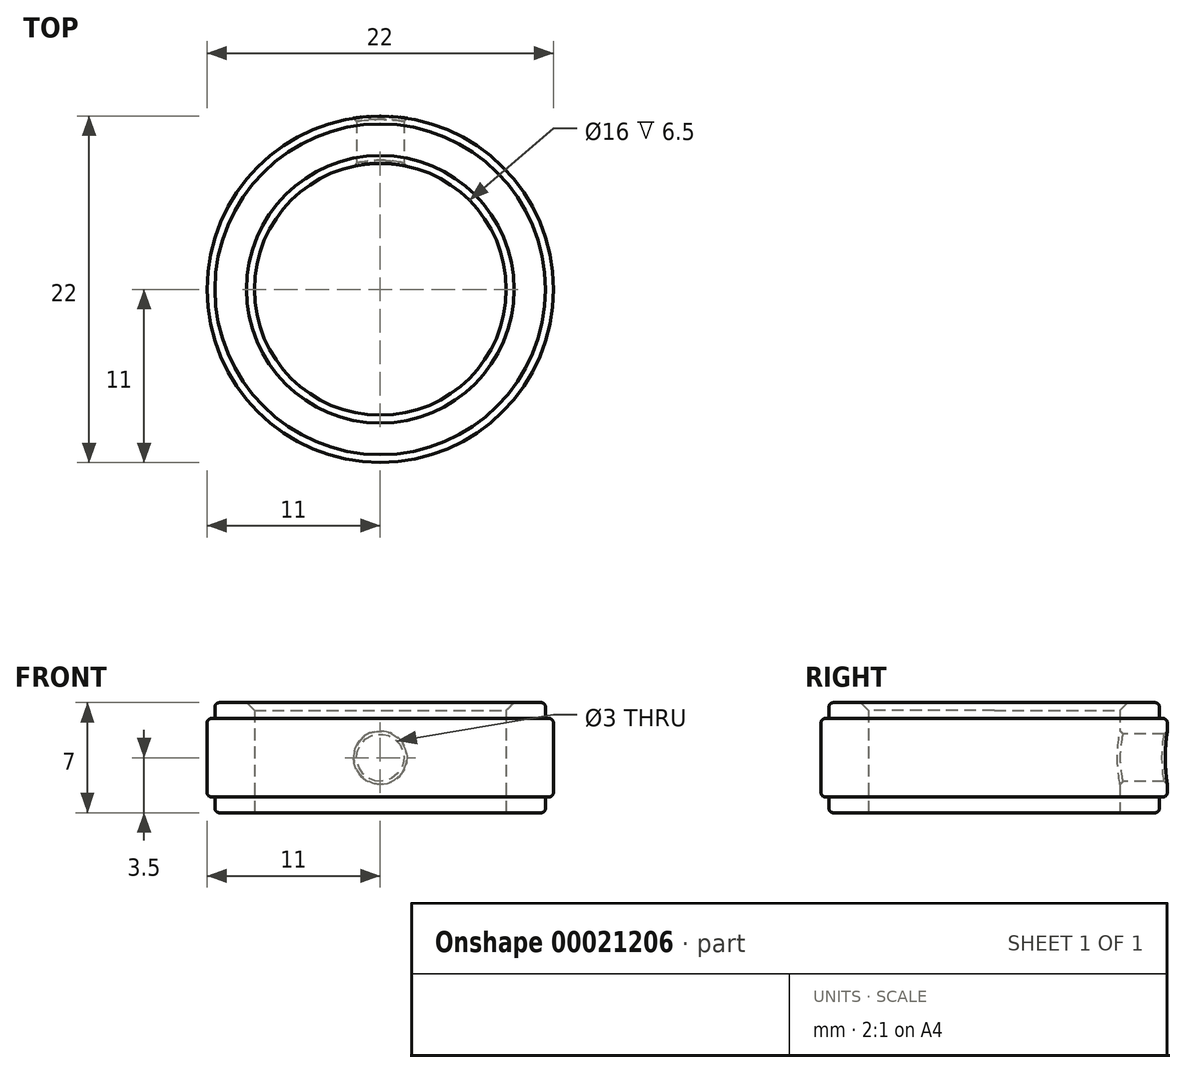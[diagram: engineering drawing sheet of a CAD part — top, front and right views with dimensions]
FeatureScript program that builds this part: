
annotation { "Feature Type Name" : "Feature", "Feature Type Description" : "" }
export const myFeature = defineFeature(function(context is Context, id is Id, definition is map)
    precondition{}
    {
        {
            var Q0;
            Q0=qCreatedBy(makeId("Top.planeOp"),FACE);
            var sketch = newSketch(context, id + "F0", { "sketchPlane" : qUnion([Q0])});
            skCircle(sketch, "E0", {"center": v(0, 0) * mm, "radius": 11 * mm});
            skSolve(sketch);
        }
        {
            var Q0;
            Q0=qSketchRegion(id+"F0",true);
            extrude(context, id + "F1", {"entities" : qUnion([Q0]), "endBound" : BoundingType.SYMMETRIC, "depth" : 5 * mm});
        }
        {
            var Q0;
            Q0=makeQuery(id+"F1.opExtrude","CAP_FACE",FACE,{"disambiguationData":[OSD([sQuery(id+"F0.wireOp",EDGE,"E0")])],"isStart":false});
            var sketch = newSketch(context, id + "F2", { "sketchPlane" : qUnion([Q0])});
            skCircle(sketch, "E1", {"center": v(0, 0) * mm, "radius": 10.5 * mm});
            skSolve(sketch);
        }
        {
            var Q0;
            Q0=qSketchRegion(id+"F2",true);
            extrude(context, id + "F3", {"entities" : qUnion([Q0]), "operationType" : NewBodyOperationType.ADD, "depth" : 1 * mm});
        }
        {
            var Q0;
            Q0=makeQuery(id+"F1.opExtrude","CAP_FACE",FACE,{"disambiguationData":[OSD([sQuery(id+"F0.wireOp",EDGE,"E0")])],"isStart":true});
            var sketch = newSketch(context, id + "F4", { "sketchPlane" : qUnion([Q0])});
            skCircle(sketch, "E2", {"center": v(0, 0) * mm, "radius": 10.5 * mm});
            skSolve(sketch);
        }
        {
            var Q0;
            Q0=qSketchRegion(id+"F4",true);
            extrude(context, id + "F5", {"entities" : qUnion([Q0]), "operationType" : NewBodyOperationType.ADD, "depth" : 1 * mm});
        }
        {
            var Q0;
            Q0=makeQuery(id+"F5.opExtrude","CAP_FACE",FACE,{"disambiguationData":[OSD([sQuery(id+"F4.wireOp",EDGE,"E2")])],"isStart":false});
            var sketch = newSketch(context, id + "F6", { "sketchPlane" : qUnion([Q0])});
            skCircle(sketch, "E3", {"center": v(0, 0) * mm, "radius": 8 * mm});
            skSolve(sketch);
        }
        {
            var Q0;
            Q0=qSketchRegion(id+"F6",true);
            extrude(context, id + "F7", {"entities" : qUnion([Q0]), "operationType" : NewBodyOperationType.REMOVE, "endBound" : BoundingType.THROUGH_ALL, "oppositeDirection" : true, "depth" : 25 * mm});
        }
        {
            var Q0;
            Q0=makeQuery(id+"F3.opExtrude","CAP_EDGE",EDGE,{"disambiguationData":[OSD([sQuery(id+"F2.wireOp",EDGE,"E1")])],"isStart":false});
            var Q1;
            Q1=makeQuery(id+"F1.opExtrude","CAP_EDGE",EDGE,{"disambiguationData":[OSD([sQuery(id+"F0.wireOp",EDGE,"E0")])],"isStart":false});
            var Q2;
            Q2=makeQuery(id+"F1.opExtrude","CAP_EDGE",EDGE,{"disambiguationData":[OSD([sQuery(id+"F0.wireOp",EDGE,"E0")])],"isStart":true});
            var Q3;
            Q3=makeQuery(id+"F5.opExtrude","CAP_EDGE",EDGE,{"disambiguationData":[OSD([sQuery(id+"F4.wireOp",EDGE,"E2")])],"isStart":false});
            fillet(context, id + "F8", {"entities" : qUnion([Q0, Q1, Q2, Q3]), "radius" : 0.3 * mm, "tangentPropagation" : true, "allowEdgeOverflow" : false});
        }
        {
            var Q0;
            Q0=makeQuery(id+"F7.boolean.opBoolean","INTERSECT",EDGE,{"derivedFrom":[makeQuery(id+"F3.opExtrude","CAP_FACE",FACE,{"disambiguationData":[OSD([sQuery(id+"F2.wireOp",EDGE,"E1")])],"isStart":false}),makeQuery(id+"F7.opExtrude","SWEPT_FACE",FACE,{"disambiguationData":[OSD([sQuery(id+"F6.wireOp",EDGE,"E3")])]})]});
            var Q1;
            Q1=makeQuery(id+"F7.boolean.opBoolean","COPY",EDGE,{"derivedFrom":makeQuery(id+"F7.opExtrude","CAP_EDGE",EDGE,{"disambiguationData":[OSD([sQuery(id+"F6.wireOp",EDGE,"E3")])],"isStart":true})});
            chamfer(context, id + "F9", {"entities" : qUnion([Q0, Q1]), "width" : 0.5 * mm, "tangentPropagation" : true});
        }
        {
            var Q0;
            Q0=qCreatedBy(makeId("Front.planeOp"),FACE);
            var sketch = newSketch(context, id + "F10", { "sketchPlane" : qUnion([Q0])});
            skCircle(sketch, "E4", {"center": v(0, 0) * mm, "radius": 1.5 * mm});
            skSolve(sketch);
        }
        {
            var Q0;
            Q0=qSketchRegion(id+"F10",true);
            extrude(context, id + "F11", {"entities" : qUnion([Q0]), "operationType" : NewBodyOperationType.REMOVE, "endBound" : BoundingType.THROUGH_ALL, "oppositeDirection" : true, "depth" : 25 * mm});
        }
        {
            var Q0;
            Q0=makeQuery(id+"F11.boolean.opBoolean","INTERSECT",EDGE,{"derivedFrom":[makeQuery(id+"F1.opExtrude","SWEPT_FACE",FACE,{"disambiguationData":[OSD([sQuery(id+"F0.wireOp",EDGE,"E0")])]}),makeQuery(id+"F11.opExtrude","SWEPT_FACE",FACE,{"disambiguationData":[OSD([sQuery(id+"F10.wireOp",EDGE,"E4")])]})]});
            var Q1;
            Q1=makeQuery(id+"F11.boolean.opBoolean","INTERSECT",EDGE,{"derivedFrom":[makeQuery(id+"F7.boolean.opBoolean","COPY",FACE,{"derivedFrom":makeQuery(id+"F7.opExtrude","SWEPT_FACE",FACE,{"disambiguationData":[OSD([sQuery(id+"F6.wireOp",EDGE,"E3")])]})}),makeQuery(id+"F11.opExtrude","SWEPT_FACE",FACE,{"disambiguationData":[OSD([sQuery(id+"F10.wireOp",EDGE,"E4")])]})]});
            chamfer(context, id + "F12", {"entities" : qUnion([Q0, Q1]), "width" : 0.2 * mm, "tangentPropagation" : true});
        }
    });
